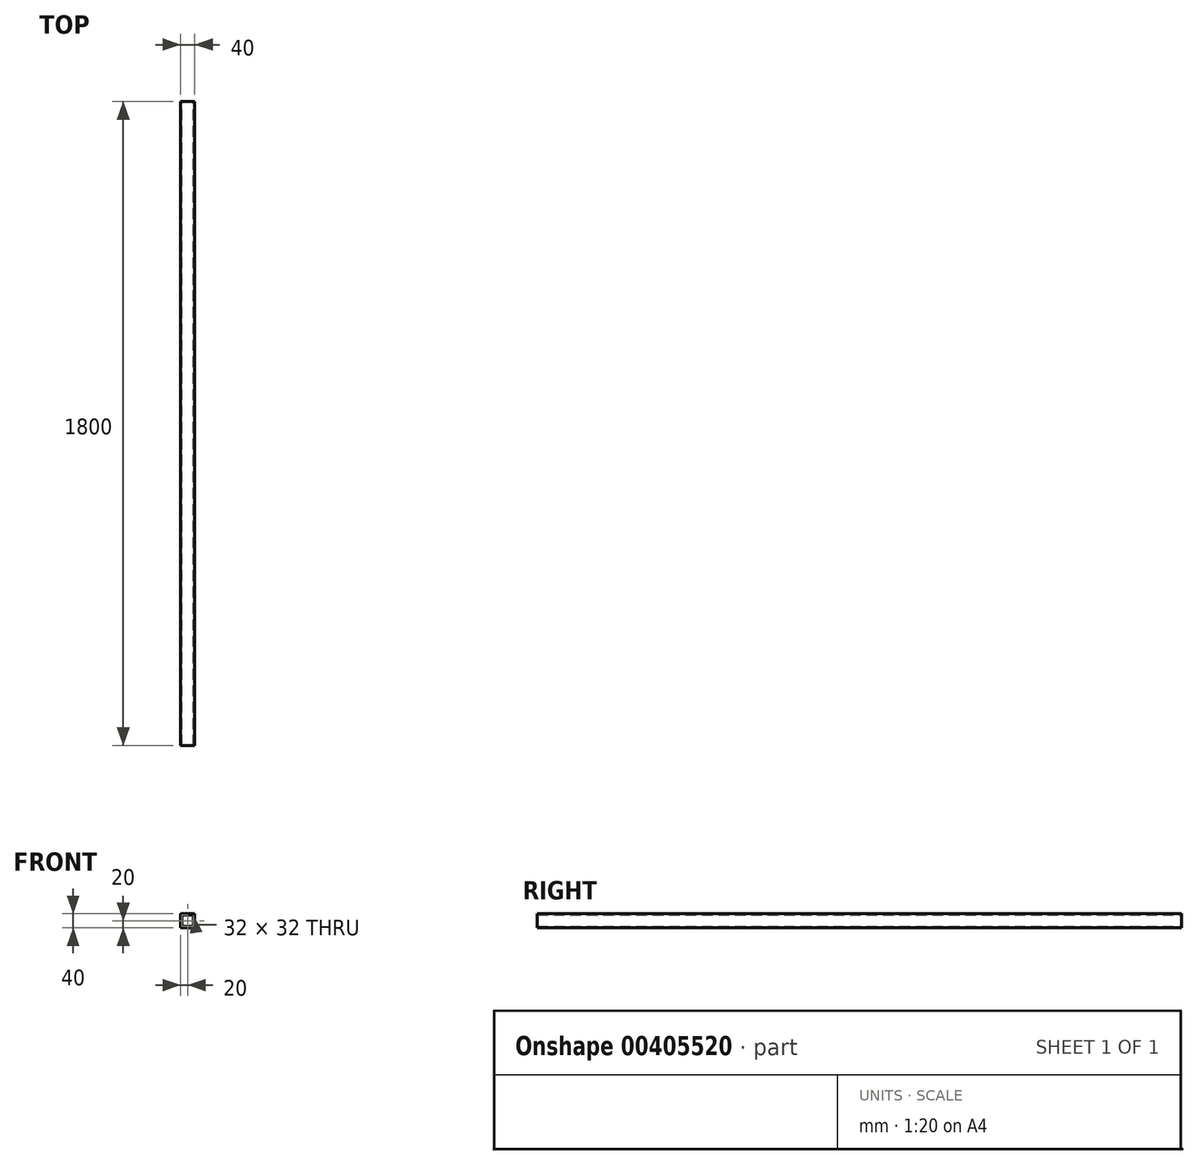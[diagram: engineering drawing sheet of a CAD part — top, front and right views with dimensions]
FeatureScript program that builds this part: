
annotation { "Feature Type Name" : "Feature", "Feature Type Description" : "" }
export const myFeature = defineFeature(function(context is Context, id is Id, definition is map)
    precondition{}
    {
        {
            var Q0;
            Q0=qCreatedBy(makeId("Front.planeOp"),FACE);
            var sketch = newSketch(context, id + "F0", { "sketchPlane" : qUnion([Q0])});
            skLineSegment(sketch, "E0.bottom", {"start": v(20, 20) * mm, "end": v(-20, 20) * mm});
            skLineSegment(sketch, "E0.top", {"start": v(20, -20) * mm, "end": v(-20, -20) * mm});
            skLineSegment(sketch, "E0.left", {"start": v(20, 20) * mm, "end": v(20, -20) * mm});
            skLineSegment(sketch, "E0.right", {"start": v(-20, 20) * mm, "end": v(-20, -20) * mm});
            skPoint(sketch, "E0.middle", {"position": v(0, 0) * mm});
            skLineSegment(sketch, "E1.0", {"start": v(16, 16) * mm, "end": v(-16, 16) * mm});
            skLineSegment(sketch, "E1.1", {"start": v(16, 16) * mm, "end": v(16, -16) * mm});
            skLineSegment(sketch, "E1.2", {"start": v(16, -16) * mm, "end": v(-16, -16) * mm});
            skLineSegment(sketch, "E1.3", {"start": v(-16, 16) * mm, "end": v(-16, -16) * mm});
            skSolve(sketch);
        }
        {
            var Q0;
            Q0 = qSketchRegion(id + "F0", true);
            extrude(context, id + "F1", {"entities" : qUnion([Q0]), "endBound" : BoundingType.SYMMETRIC, "depth" : 1800 * mm});
        }
    });
